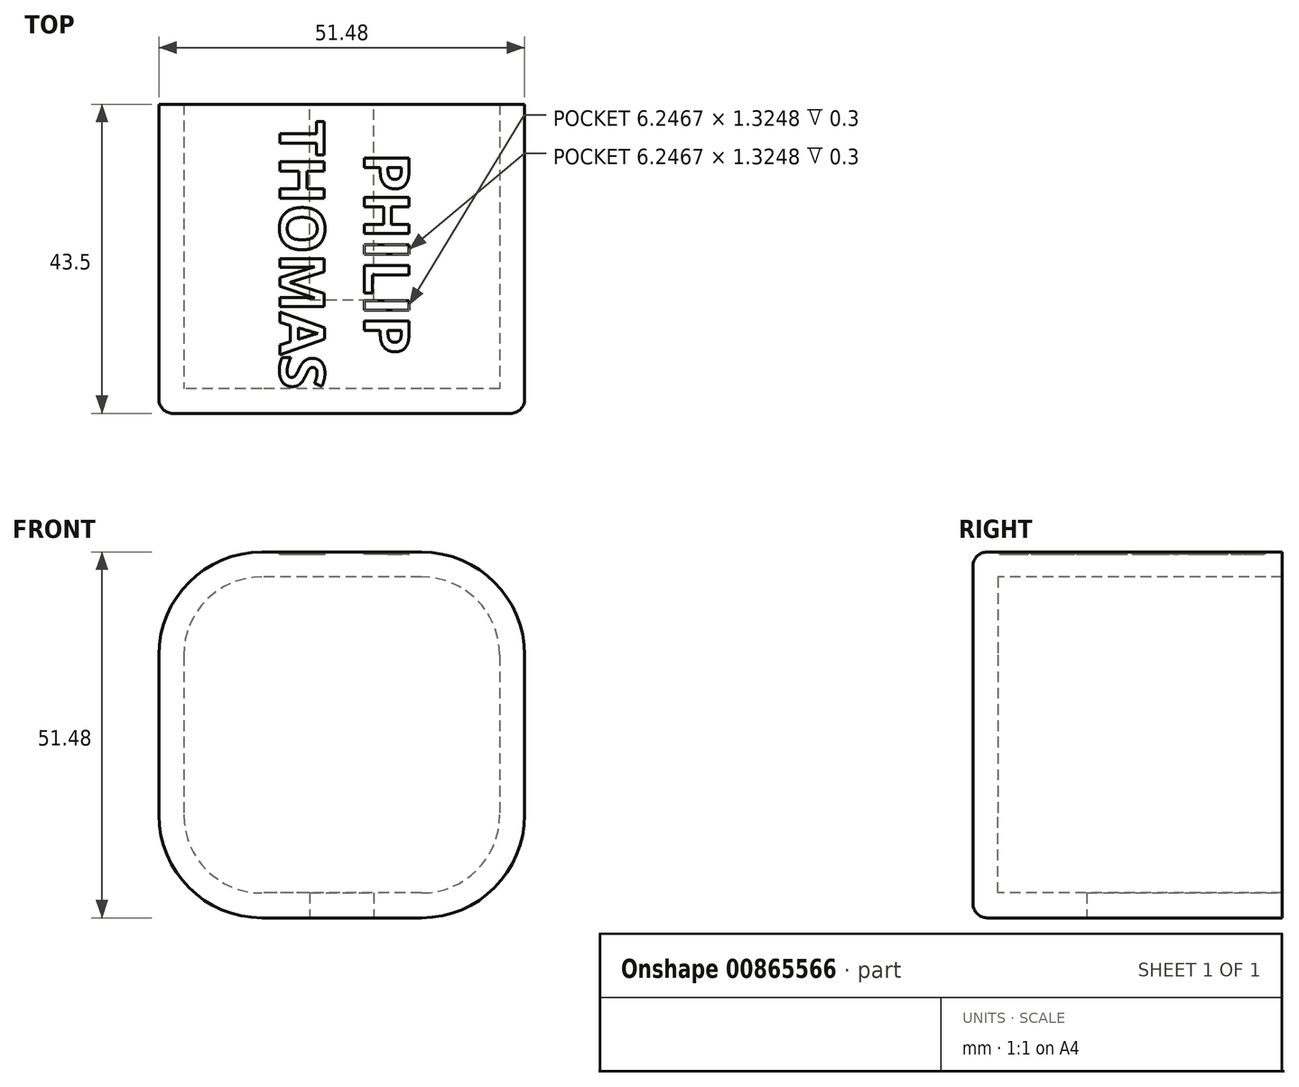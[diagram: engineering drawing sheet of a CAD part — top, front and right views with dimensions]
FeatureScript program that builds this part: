
annotation { "Feature Type Name" : "Feature", "Feature Type Description" : "" }
export const myFeature = defineFeature(function(context is Context, id is Id, definition is map)
    precondition{}
    {
        {
            var Q0;
            Q0=qCreatedBy(makeId("Front.planeOp"),FACE);
            var sketch = newSketch(context, id + "F0", { "sketchPlane" : qUnion([Q0])});
            skLineSegment(sketch, "E0.bottom", {"start": v(22.24, 22.24) * mm, "end": v(-22.24, 22.24) * mm});
            skLineSegment(sketch, "E0.top", {"start": v(22.24, -22.24) * mm, "end": v(-22.24, -22.24) * mm});
            skLineSegment(sketch, "E0.left", {"start": v(22.24, 22.24) * mm, "end": v(22.24, -22.24) * mm});
            skLineSegment(sketch, "E0.right", {"start": v(-22.24, 22.24) * mm, "end": v(-22.24, -22.24) * mm});
            skPoint(sketch, "E0.middle", {"position": v(0, 0) * mm});
            skSolve(sketch);
        }
        {
            var Q0;
            Q0 = qSketchRegion(id + "F0", true);
            extrude(context, id + "F1", {"entities" : qUnion([Q0]), "oppositeDirection" : true, "depth" : 40 * mm, "offsetDistance" : 25 * mm});
        }
        {
            var Q0;
            Q0=makeQuery(id+"F1.opExtrude","SWEPT_EDGE",EDGE,{"disambiguationData":[OSD([sQuery(id+"F0.wireOp",EDGE,"E0.bottom"),sQuery(id+"F0.wireOp",EDGE,"E0.left")])]});
            var Q1;
            Q1=makeQuery(id+"F1.opExtrude","SWEPT_EDGE",EDGE,{"disambiguationData":[OSD([sQuery(id+"F0.wireOp",EDGE,"E0.bottom"),sQuery(id+"F0.wireOp",EDGE,"E0.right")])]});
            var Q2;
            Q2=makeQuery(id+"F1.opExtrude","SWEPT_EDGE",EDGE,{"disambiguationData":[OSD([sQuery(id+"F0.wireOp",EDGE,"E0.top"),sQuery(id+"F0.wireOp",EDGE,"E0.left")])]});
            var Q3;
            Q3=makeQuery(id+"F1.opExtrude","SWEPT_EDGE",EDGE,{"disambiguationData":[OSD([sQuery(id+"F0.wireOp",EDGE,"E0.top"),sQuery(id+"F0.wireOp",EDGE,"E0.right")])]});
            fillet(context, id + "F2", {"entities" : qUnion([Q0, Q1, Q2, Q3]), "radius" : 11 * mm, "tangentPropagation" : true, "defaultsChanged" : true, "vertexSettings" : [], "allowEdgeOverflow" : false});
        }
        {
            var Q0;
            Q0=makeQuery(id+"F1.opExtrude","CAP_FACE",FACE,{"disambiguationData":[OSD([sQuery(id+"F0.wireOp",EDGE,"E0.bottom"),sQuery(id+"F0.wireOp",EDGE,"E0.top"),sQuery(id+"F0.wireOp",EDGE,"E0.left"),sQuery(id+"F0.wireOp",EDGE,"E0.right")])],"isStart":false});
            shell(context, id + "F3", {"entities" : qUnion([Q0]), "thickness" : 3.5 * mm, "oppositeDirection" : true});
        }
        {
            var Q0;
            Q0=makeQuery(id+"F1.opExtrude","CAP_FACE",FACE,{"disambiguationData":[OSD([sQuery(id+"F0.wireOp",EDGE,"E0.bottom"),sQuery(id+"F0.wireOp",EDGE,"E0.top"),sQuery(id+"F0.wireOp",EDGE,"E0.left"),sQuery(id+"F0.wireOp",EDGE,"E0.right")])],"isStart":false});
            var sketch = newSketch(context, id + "F4", { "sketchPlane" : qUnion([Q0])});
            skLineSegment(sketch, "E1.bottom", {"start": v(4.5, 8.58) * mm, "end": v(-4.5, 8.58) * mm});
            skLineSegment(sketch, "E1.top", {"start": v(4.5, -39.48) * mm, "end": v(-4.5, -39.48) * mm});
            skLineSegment(sketch, "E1.left", {"start": v(4.5, 8.58) * mm, "end": v(4.5, -39.48) * mm});
            skLineSegment(sketch, "E1.right", {"start": v(-4.5, 8.58) * mm, "end": v(-4.5, -39.48) * mm});
            skPoint(sketch, "E1.middle", {"position": v(0, -15.45) * mm});
            skSolve(sketch);
        }
        {
            var Q0;
            Q0 = qSketchRegion(id + "F4", true);
            var Q1;
            Q1=makeQuery(id+"F1.opExtrude","CAP_FACE",FACE,{"disambiguationData":[OSD([sQuery(id+"F0.wireOp",EDGE,"E0.bottom"),sQuery(id+"F0.wireOp",EDGE,"E0.top"),sQuery(id+"F0.wireOp",EDGE,"E0.left"),sQuery(id+"F0.wireOp",EDGE,"E0.right")])],"isStart":true});
            extrude(context, id + "F5", {"entities" : qUnion([Q0]), "operationType" : NewBodyOperationType.REMOVE, "endBound" : BoundingType.UP_TO_SURFACE, "oppositeDirection" : true, "depth" : 25 * mm, "endBoundEntityFace" : qUnion([Q1]), "hasOffset" : true, "offsetDistance" : 16 * mm});
        }
        {
            var Q0;
            Q0=makeQuery(id+"F1.opExtrude","CAP_FACE",FACE,{"disambiguationData":[OSD([sQuery(id+"F0.wireOp",EDGE,"E0.bottom"),sQuery(id+"F0.wireOp",EDGE,"E0.top"),sQuery(id+"F0.wireOp",EDGE,"E0.left"),sQuery(id+"F0.wireOp",EDGE,"E0.right")])],"isStart":true});
            var Q1;
            Q1=makeQuery(id+"F5.boolean.opBoolean","COPY",EDGE,{"derivedFrom":makeQuery(id+"F5.opExtrude","CAP_EDGE",EDGE,{"disambiguationData":[OSD([sQuery(id+"F4.wireOp",EDGE,"E1.left")])],"isStart":true})});
            var Q2;
            Q2=makeQuery(id+"F5.boolean.opBoolean","COPY",EDGE,{"derivedFrom":makeQuery(id+"F5.opExtrude","CAP_EDGE",EDGE,{"disambiguationData":[OSD([sQuery(id+"F4.wireOp",EDGE,"E1.right")])],"isStart":true})});
            fillet(context, id + "F6", {"entities" : qUnion([Q0, Q1, Q2]), "radius" : 2 * mm, "tangentPropagation" : true, "allowEdgeOverflow" : false});
        }
        {
            var Q0;
            Q0=makeQuery(id+"F1.opExtrude","SWEPT_FACE",FACE,{"disambiguationData":[OSD([sQuery(id+"F0.wireOp",EDGE,"E0.bottom")])]});
            var sketch = newSketch(context, id + "F7", { "sketchPlane" : qUnion([Q0])});
            skText(sketch, "E2", { "text": "  PHILIP \nTHOMAS", "fontName": "OpenSans-Bold.ttf"});
            const initialGuessF7  = {"E2": [0.0032, 0.03775, 0, -1, 0.0063]};
            skSetInitialGuess(sketch, initialGuessF7);
            skSolve(sketch);
        }
        {
            var Q0;
            Q0 = qSketchRegion(id + "F7", true);
            extrude(context, id + "F8", {"entities" : qUnion([Q0]), "operationType" : NewBodyOperationType.REMOVE, "flatOperationType" : FlatOperationType.REMOVE, "oppositeDirection" : true, "depth" : 0.3 * mm, "offsetDistance" : 25 * mm, "domain" : OperationDomain.MODEL});
        }
    });
